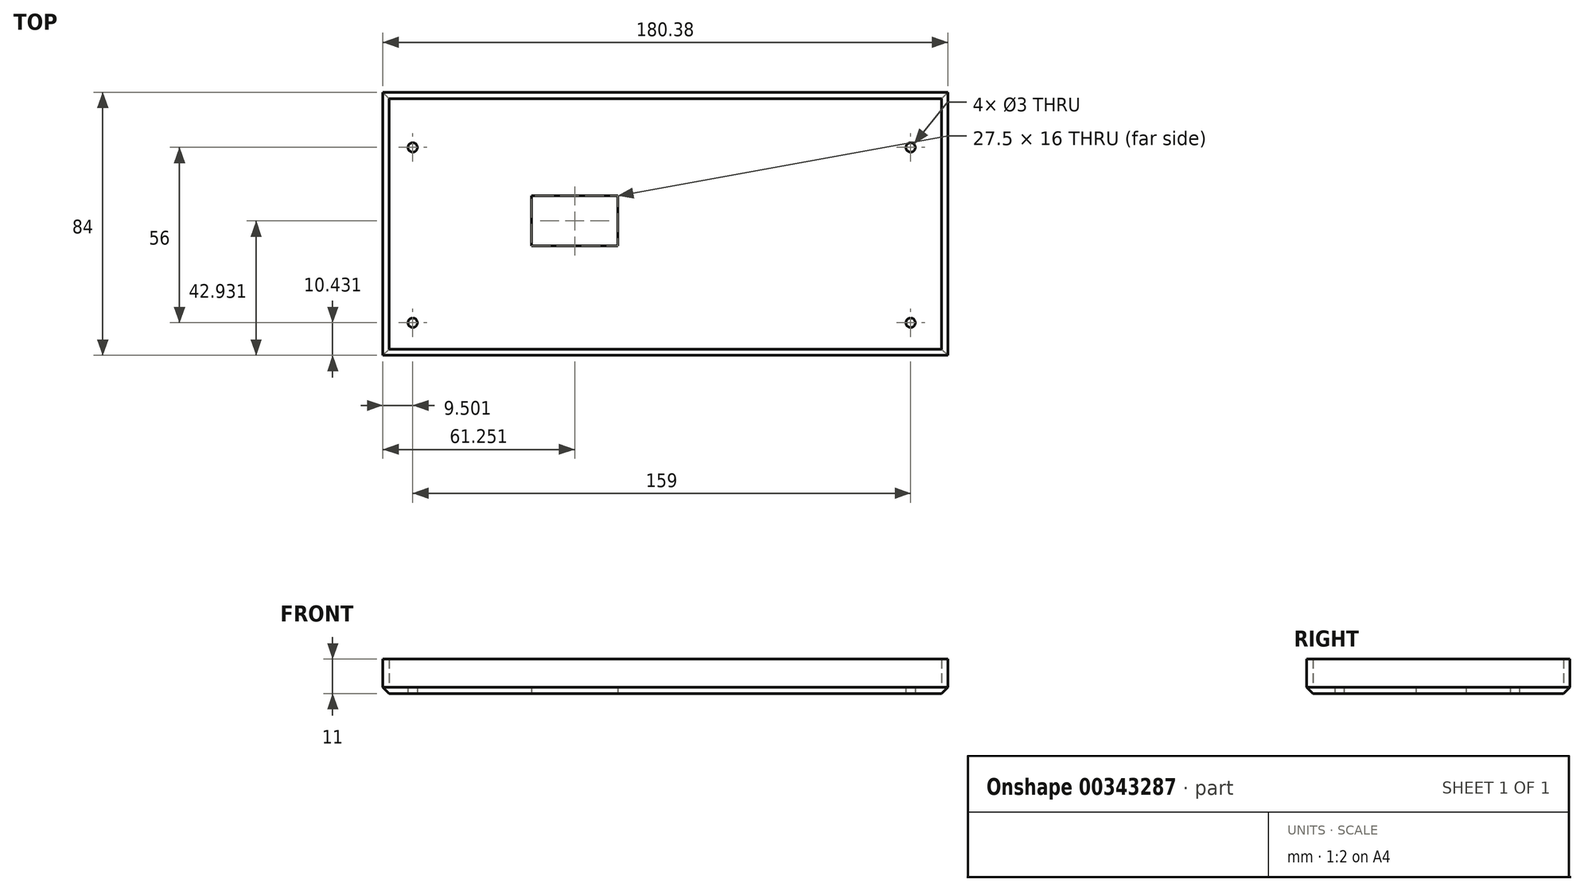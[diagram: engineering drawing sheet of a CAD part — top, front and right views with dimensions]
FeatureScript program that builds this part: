
annotation { "Feature Type Name" : "Feature", "Feature Type Description" : "" }
export const myFeature = defineFeature(function(context is Context, id is Id, definition is map)
    precondition{}
    {
        {
            var Q0;
            Q0=qCreatedBy(makeId("Top.planeOp"),FACE);
            var sketch = newSketch(context, id + "F0", { "sketchPlane" : qUnion([Q0])});
            skLineSegment(sketch, "E0.bottom", {"start": v(0, 0) * mm, "end": v(-180.38, 0) * mm});
            skLineSegment(sketch, "E0.top", {"start": v(0, 84) * mm, "end": v(-180.38, 84) * mm});
            skLineSegment(sketch, "E0.left", {"start": v(0, 0) * mm, "end": v(0, 84) * mm});
            skLineSegment(sketch, "E0.right", {"start": v(-180.38, 0) * mm, "end": v(-180.38, 84) * mm});
            skLineSegment(sketch, "E1.bottom", {"start": v(-178.38, 82) * mm, "end": v(-2, 82) * mm});
            skLineSegment(sketch, "E1.top", {"start": v(-178.38, 2) * mm, "end": v(-2, 2) * mm});
            skLineSegment(sketch, "E1.left", {"start": v(-178.38, 82) * mm, "end": v(-178.38, 2) * mm});
            skLineSegment(sketch, "E1.right", {"start": v(-2, 82) * mm, "end": v(-2, 2) * mm});
            skLineSegment(sketch, "E2.bottom", {"start": v(-173.38, 68.93) * mm, "end": v(-7.2, 68.93) * mm});
            skLineSegment(sketch, "E3", {"start": v(-173.38, 68.93) * mm, "end": v(-173.38, 7.93) * mm});
            skLineSegment(sketch, "E4", {"start": v(-173.38, 7.93) * mm, "end": v(-9.38, 7.93) * mm});
            skLineSegment(sketch, "E5", {"start": v(-9.38, 7.93) * mm, "end": v(-9.38, 68.93) * mm});
            skLineSegment(sketch, "E6.bottom", {"start": v(-170.88, 66.43) * mm, "end": v(-11.88, 66.43) * mm});
            skLineSegment(sketch, "E6.top", {"start": v(-170.88, 10.43) * mm, "end": v(-11.88, 10.43) * mm});
            skLineSegment(sketch, "E6.left", {"start": v(-170.88, 66.43) * mm, "end": v(-170.88, 10.43) * mm});
            skLineSegment(sketch, "E6.right", {"start": v(-11.88, 66.43) * mm, "end": v(-11.88, 10.43) * mm});
            skCircle(sketch, "E7", {"center": v(-170.88, 10.43) * mm, "radius": 1.5 * mm});
            skCircle(sketch, "E8", {"center": v(-170.88, 66.43) * mm, "radius": 1.5 * mm});
            skCircle(sketch, "E9", {"center": v(-11.88, 66.43) * mm, "radius": 1.5 * mm});
            skCircle(sketch, "E10", {"center": v(-11.88, 10.43) * mm, "radius": 1.5 * mm});
            skLineSegment(sketch, "E11.bottom", {"start": v(-132.88, 50.93) * mm, "end": v(-105.38, 50.93) * mm});
            skLineSegment(sketch, "E11.top", {"start": v(-132.88, 34.93) * mm, "end": v(-105.38, 34.93) * mm});
            skLineSegment(sketch, "E11.left", {"start": v(-132.88, 50.93) * mm, "end": v(-132.88, 34.93) * mm});
            skLineSegment(sketch, "E11.right", {"start": v(-105.38, 50.93) * mm, "end": v(-105.38, 34.93) * mm});
            skSolve(sketch);
        }
        {
            var Q0;
            Q0 = qSketchRegion(id + "F0", true);
            extrude(context, id + "F1", {"entities" : qUnion([Q0]), "depth" : 11 * mm});
        }
        {
            var Q0;
            Q0=makeQuery(id+"F0.imprint","IMPRINT",FACE,{"disambiguationData":[TD([[makeQuery(id+"F0.imprint","IMPRINT",EDGE,{"derivedFrom":sQuery(id+"F0.wireOp",EDGE,"E1.bottom")}),-1.0]])]});
            var Q1;
            Q1=makeQuery(id+"F0.imprint","IMPRINT",FACE,{"disambiguationData":[TD([[makeQuery(id+"F0.imprint","IMPRINT",EDGE,{"derivedFrom":sQuery(id+"F0.wireOp",EDGE,"E11.bottom")}),1.0]])]});
            var Q2;
            {var subQ13=sQuery(id+"F0.wireOp",EDGE,"E3");Q2=makeQuery(id+"F0.imprint","IMPRINT",FACE,{"disambiguationData":[TD([[makeQuery(id+"F0.imprint","IMPRINT",EDGE,{"derivedFrom":subQ13}),1.0]])]});}
            extrude(context, id + "F2", {"entities" : qUnion([Q0, Q1, Q2]), "operationType" : NewBodyOperationType.ADD, "depth" : 2 * mm});
        }
        {
            var Q0;
            Q0=makeQuery(id+"F1.opExtrude","CAP_EDGE",EDGE,{"disambiguationData":[OSD([sQuery(id+"F0.wireOp",EDGE,"E0.left")])],"isStart":true});
            var Q1;
            Q1=makeQuery(id+"F1.opExtrude","CAP_EDGE",EDGE,{"disambiguationData":[OSD([sQuery(id+"F0.wireOp",EDGE,"E0.top")])],"isStart":true});
            var Q2;
            Q2=makeQuery(id+"F1.opExtrude","CAP_EDGE",EDGE,{"disambiguationData":[OSD([sQuery(id+"F0.wireOp",EDGE,"E0.bottom")])],"isStart":true});
            var Q3;
            Q3=makeQuery(id+"F1.opExtrude","CAP_EDGE",EDGE,{"disambiguationData":[OSD([sQuery(id+"F0.wireOp",EDGE,"E0.right")])],"isStart":true});
            chamfer(context, id + "F3", {"entities" : qUnion([Q0, Q1, Q2, Q3]), "width" : 2 * mm, "tangentPropagation" : true});
        }
    });
